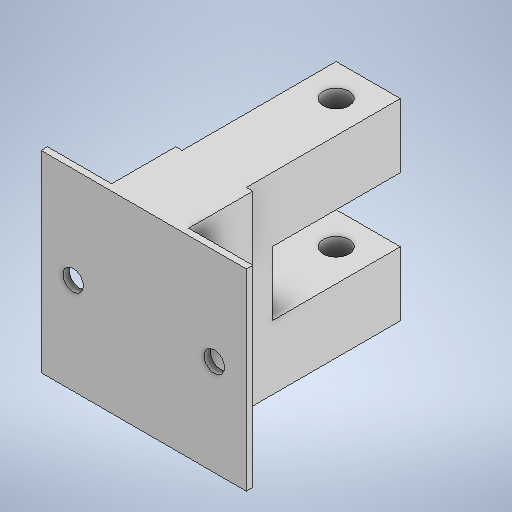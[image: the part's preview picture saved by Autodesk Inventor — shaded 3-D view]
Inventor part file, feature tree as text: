
AUTODESK INVENTOR PART (.ipt)
format: ipt  version: 2025 (Build 290162000, 162)  size: 273,920 bytes
history: native  units: mm
features: sketch x4, projected_geometry x3, extrude x2, hole x2, other x1, mirror x1
ambient origin geometry x8: Origin, YZ Plane, XZ Plane, XY Plane, X Axis, Y Axis, Z Axis, Center Point
bodies: Body1 (feature_tree)
feature tree (13):
  other  "Těleso1"
  extrude  "Vysunutí1"  Depth=10.0mm
  mirror  "Zrcadlit1"
  extrude  "Vysunutí3"  Depth=10.0mm
  hole  "Díra1"  [1 undecoded]
  hole  "Díra2"  [1 undecoded]
  sketch  "Náčrt1"
  sketch  "Náčrt2"
  projected_geometry  "Promítnutá smyčka1"
  sketch  "Náčrt3"
  projected_geometry  "Promítnutá smyčka2"
  sketch  "Náčrt4"
  projected_geometry  "Promítnutá smyčka3"
note: 2 required parameter values undecoded (feature->parameter linkage not recoverable at this tier; creation-order binding heuristic only, values carry confidence <= 0.55)
